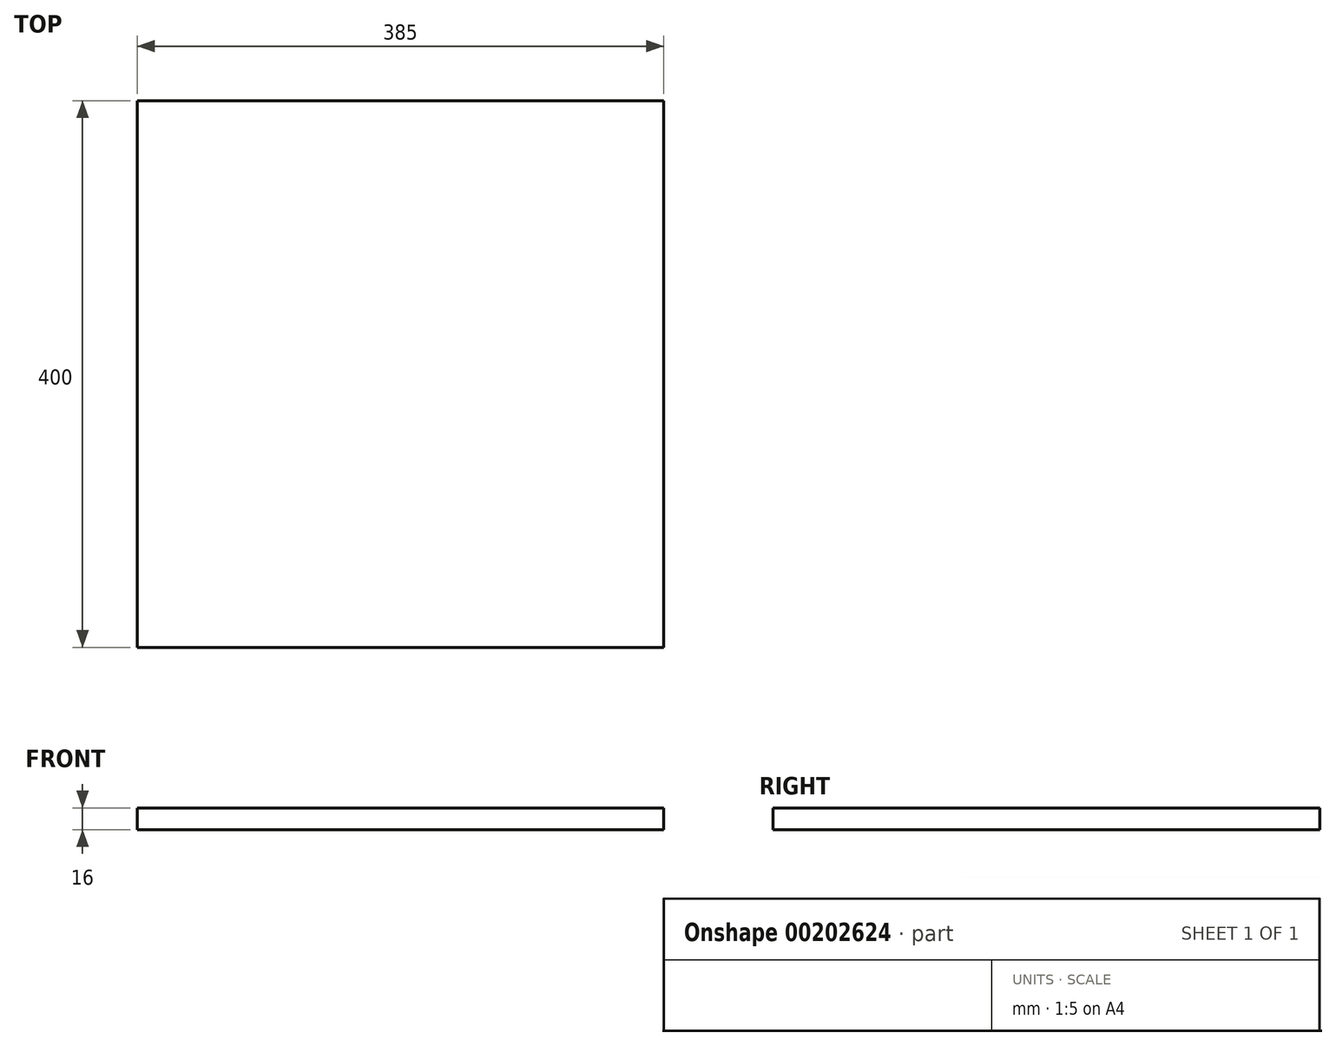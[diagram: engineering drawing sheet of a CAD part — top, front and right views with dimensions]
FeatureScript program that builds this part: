
annotation { "Feature Type Name" : "Feature", "Feature Type Description" : "" }
export const myFeature = defineFeature(function(context is Context, id is Id, definition is map)
    precondition{}
    {
        {
            var Q0;
            Q0=qCreatedBy(makeId("Top.planeOp"),FACE);
            var sketch = newSketch(context, id + "F0", { "sketchPlane" : qUnion([Q0])});
            skLineSegment(sketch, "E0.bottom", {"start": v(-864.34, -235.28) * mm, "end": v(-479.34, -235.28) * mm});
            skLineSegment(sketch, "E0.top", {"start": v(-864.34, 164.72) * mm, "end": v(-479.34, 164.72) * mm});
            skLineSegment(sketch, "E0.left", {"start": v(-864.34, -235.28) * mm, "end": v(-864.34, 164.72) * mm});
            skLineSegment(sketch, "E0.right", {"start": v(-479.34, -235.28) * mm, "end": v(-479.34, 164.72) * mm});
            skSolve(sketch);
        }
        {
            var Q0;
            Q0=makeQuery(id+"F0.imprint","IMPRINT",FACE,{"disambiguationData":[TD([[makeQuery(id+"F0.imprint","IMPRINT",EDGE,{"derivedFrom":sQuery(id+"F0.wireOp",EDGE,"E0.bottom")}),1.0]])]});
            extrude(context, id + "F1", {"entities" : qUnion([Q0]), "depth" : 16 * mm});
        }
    });
